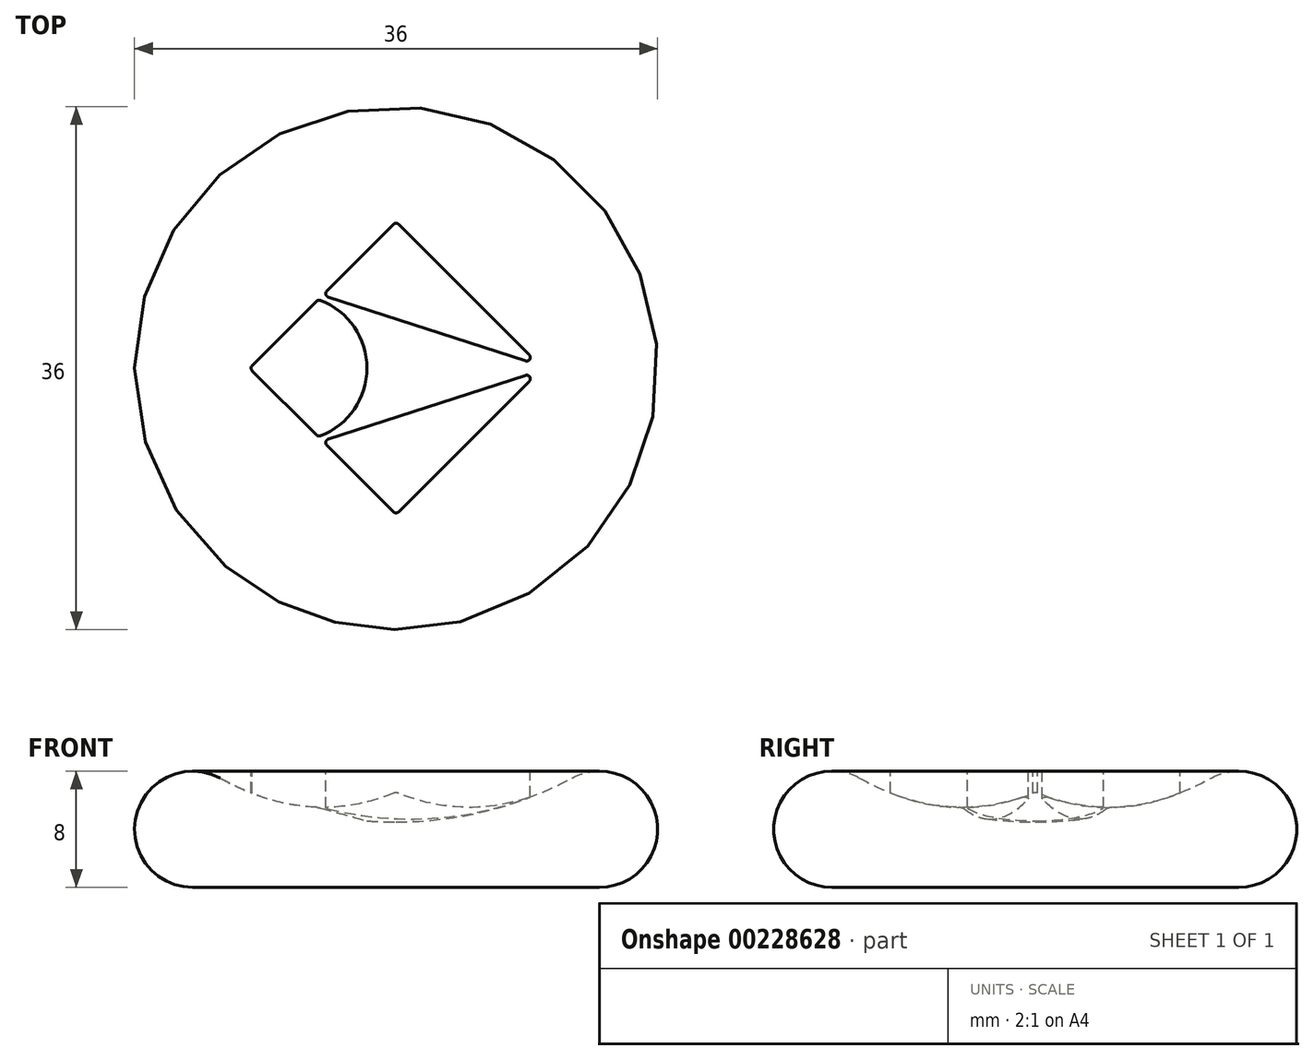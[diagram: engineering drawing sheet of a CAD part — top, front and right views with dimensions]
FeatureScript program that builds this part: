
annotation { "Feature Type Name" : "Feature", "Feature Type Description" : "" }
export const myFeature = defineFeature(function(context is Context, id is Id, definition is map)
    precondition{}
    {
        {
            var Q0;
            Q0=qCreatedBy(makeId("Front.planeOp"),FACE);
            var sketch = newSketch(context, id + "F0", { "sketchPlane" : qUnion([Q0])});
            skCircle(sketch, "E0", {"center": v(-14, 4) * mm, "radius": 4 * mm});
            skLineSegment(sketch, "E1", {"start": v(-14, 0) * mm, "end": v(0, 0) * mm});
            skLineSegment(sketch, "E2", {"start": v(0, 0) * mm, "end": v(0, 4.5) * mm});
            skArc(sketch, "E3", {"start": v(-12.12, 7.53) * mm, "mid": v(-6.25, 5.27) * mm, "end": v(0, 4.5) * mm});
            skLineSegment(sketch, "E4", {"start": v(-18, 17.02) * mm, "end": v(-18, -12.9) * mm, "construction": true});
            skSolve(sketch);
        }
        {
            var Q0;
            Q0 = qSketchRegion(id + "F0", true);
            var Q1;
            Q1=sQuery(id+"F0.wireOp",EDGE,"E2");
            revolve(context, id + "F1", {"entities" : qUnion([Q0]), "axis" : qUnion([Q1]), "revolveType" : RevolveType.FULL});
        }
        {
            var Q0;
            Q0=qCreatedBy(makeId("Top.planeOp"),FACE);
            cPlane(context, id + "F2", {"entities" : qUnion([Q0]), "cplaneType" : CPlaneType.OFFSET, "offset" : 8 * mm, "width" : 150 * mm, "height" : 150 * mm});
        }
        {
            var Q0;
            Q0=qCreatedBy(id+"F2.planeOp",FACE);
            var sketch = newSketch(context, id + "F3", { "sketchPlane" : qUnion([Q0])});
            skLineSegment(sketch, "E5.bottom", {"start": v(9.16, 0.91) * mm, "end": v(0.18, 9.9) * mm});
            skLineSegment(sketch, "E5.top", {"start": v(-0.18, -9.9) * mm, "end": v(-4.77, -5.3) * mm});
            skLineSegment(sketch, "E5.left", {"start": v(9.16, -0.91) * mm, "end": v(0.18, -9.9) * mm});
            skLineSegment(sketch, "E5.right", {"start": v(-0.18, 9.9) * mm, "end": v(-4.77, 5.3) * mm});
            skPoint(sketch, "E5.middle", {"position": v(0, 0) * mm});
            skPoint(sketch, "E6.visualSharp", {"position": v(0, 10.08) * mm});
            skArc(sketch, "E6.filletArc", {"start": v(0.18, 9.9) * mm, "mid": v(0, 9.97) * mm, "end": v(-0.18, 9.9) * mm});
            skPoint(sketch, "E7.visualSharp", {"position": v(0, -10.08) * mm});
            skArc(sketch, "E7.filletArc", {"start": v(-0.18, -9.9) * mm, "mid": v(0, -9.97) * mm, "end": v(0.18, -9.9) * mm});
            skPoint(sketch, "E8.visualSharp", {"position": v(-10.08, 0) * mm});
            skArc(sketch, "E8.filletArc", {"start": v(-9.93, 0.14) * mm, "mid": v(-9.97, -0.02) * mm, "end": v(-9.9, -0.18) * mm});
            skArc(sketch, "E9", {"start": v(-5.2, -4.67) * mm, "mid": v(-2, 0) * mm, "end": v(-5.2, 4.67) * mm});
            skLineSegment(sketch, "E10.trimOffspring", {"start": v(-5.47, 4.6) * mm, "end": v(-9.93, 0.14) * mm});
            skLineSegment(sketch, "E11.trimOffspring", {"start": v(-5.47, -4.6) * mm, "end": v(-9.9, -0.18) * mm});
            skPoint(sketch, "E12.visualSharp", {"position": v(-5.06, 5.02) * mm});
            skPoint(sketch, "E13.visualSharp", {"position": v(-5.35, 4.72) * mm});
            skArc(sketch, "E13.filletArc", {"start": v(-5.2, 4.67) * mm, "mid": v(-5.34, 4.68) * mm, "end": v(-5.47, 4.6) * mm});
            skPoint(sketch, "E14.visualSharp", {"position": v(-5.35, -4.72) * mm});
            skArc(sketch, "E14.filletArc", {"start": v(-5.47, -4.6) * mm, "mid": v(-5.34, -4.68) * mm, "end": v(-5.2, -4.67) * mm});
            skPoint(sketch, "E15.visualSharp", {"position": v(-5.06, -5.02) * mm});
            skPoint(sketch, "E16.visualSharp", {"position": v(10.08, 0) * mm});
            skLineSegment(sketch, "E17", {"start": v(-4.67, 4.9) * mm, "end": v(8.91, 0.5) * mm});
            skLineSegment(sketch, "E18", {"start": v(-4.67, -4.9) * mm, "end": v(8.91, -0.5) * mm});
            skPoint(sketch, "E19.visualSharp", {"position": v(9.9, 0.18) * mm});
            skArc(sketch, "E19.filletArc", {"start": v(8.91, 0.5) * mm, "mid": v(9.2, 0.6) * mm, "end": v(9.16, 0.91) * mm});
            skPoint(sketch, "E20.visualSharp", {"position": v(9.9, -0.18) * mm});
            skArc(sketch, "E20.filletArc", {"start": v(9.16, -0.91) * mm, "mid": v(9.2, -0.6) * mm, "end": v(8.91, -0.5) * mm});
            skArc(sketch, "E21.filletArc", {"start": v(-4.67, -4.9) * mm, "mid": v(-4.83, -5.07) * mm, "end": v(-4.77, -5.3) * mm});
            skArc(sketch, "E22.filletArc", {"start": v(-4.77, 5.3) * mm, "mid": v(-4.83, 5.07) * mm, "end": v(-4.67, 4.9) * mm});
            skSolve(sketch);
        }
        {
            var Q0;
            Q0 = qSketchRegion(id + "F3", true);
            extrude(context, id + "F4", {"entities" : qUnion([Q0]), "operationType" : NewBodyOperationType.ADD, "oppositeDirection" : true, "depth" : 8 * mm});
        }
    });
